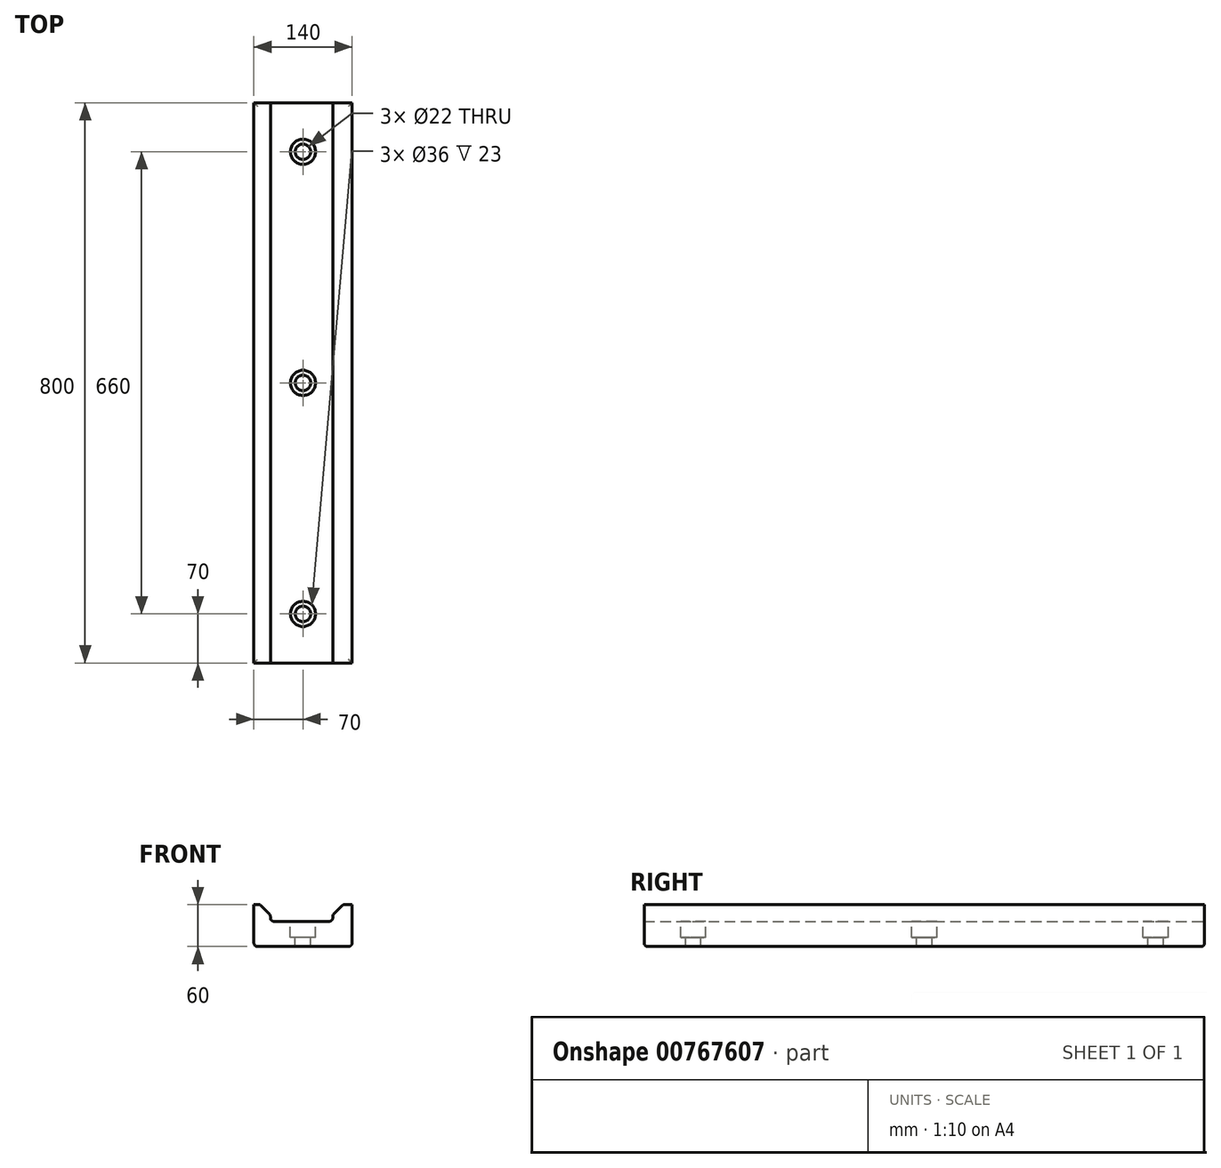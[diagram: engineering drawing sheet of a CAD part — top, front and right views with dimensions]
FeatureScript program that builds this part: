
annotation { "Feature Type Name" : "Feature", "Feature Type Description" : "" }
export const myFeature = defineFeature(function(context is Context, id is Id, definition is map)
    precondition{}
    {
        {
            var Q0;
            Q0=qCreatedBy(makeId("Front.planeOp"),FACE);
            var sketch = newSketch(context, id + "F0", { "sketchPlane" : qUnion([Q0])});
            skLineSegment(sketch, "E0.bottom", {"start": v(70, 30) * mm, "end": v(-70, 30) * mm});
            skLineSegment(sketch, "E0.top", {"start": v(70, -30) * mm, "end": v(-70, -30) * mm});
            skLineSegment(sketch, "E0.left", {"start": v(70, 30) * mm, "end": v(70, -30) * mm});
            skLineSegment(sketch, "E0.right", {"start": v(-70, 30) * mm, "end": v(-70, -30) * mm});
            skPoint(sketch, "E0.middle", {"position": v(0, 0) * mm});
            skLineSegment(sketch, "E1", {"start": v(-46.5, 6) * mm, "end": v(-46.5, 30) * mm});
            skLineSegment(sketch, "E2", {"start": v(42.5, 30) * mm, "end": v(42.5, 6) * mm});
            skLineSegment(sketch, "E3", {"start": v(-46.5, 6) * mm, "end": v(42.5, 6) * mm});
            skSolve(sketch);
        }
        {
            var Q0;
            Q0=makeQuery(id+"F0.imprint","IMPRINT",FACE,{"disambiguationData":[TD([[makeQuery(id+"F0.imprint","IMPRINT",EDGE,{"derivedFrom":sQuery(id+"F0.wireOp",EDGE,"E0.top")}),-1.0]])]});
            extrude(context, id + "F1", {"entities" : qUnion([Q0]), "depth" : 800 * mm, "offsetDistance" : 25 * mm});
        }
        {
            var Q0;
            Q0=makeQuery(id+"F1.opExtrude","SWEPT_EDGE",EDGE,{"disambiguationData":[OSD([sQuery(id+"F0.wireOp",EDGE,"E0.bottom"),sQuery(id+"F0.wireOp",EDGE,"E1")])]});
            var Q1;
            Q1=makeQuery(id+"F1.opExtrude","SWEPT_EDGE",EDGE,{"disambiguationData":[OSD([sQuery(id+"F0.wireOp",EDGE,"E0.bottom"),sQuery(id+"F0.wireOp",EDGE,"E2")])]});
            chamfer(context, id + "F2", {"entities" : qUnion([Q0, Q1]), "width" : 15 * mm, "tangentPropagation" : true});
        }
        {
            var Q0;
            {var subQ0=sQuery(id+"F0.wireOp",EDGE,"E0.bottom");var subQ1=sQuery(id+"F0.wireOp",EDGE,"E1");Q0=makeQuery(id+"F2.opChamfer","BLEND_EDGE",EDGE,{"blendedFrom":[makeQuery(id+"F1.opExtrude","SWEPT_EDGE",EDGE,{"disambiguationData":[OSD([subQ0,subQ1])]}),makeQuery(id+"F1.opExtrude","SWEPT_FACE",FACE,{"disambiguationData":[OSD([subQ0]),TDD([makeQuery(id+"F0.imprint","IMPRINT",EDGE,{"disambiguationData":[TD([[makeQuery(id+"F0.imprint","INTERSECT",VERTEX,{"derivedFrom":[subQ0,sQuery(id+"F0.wireOp",EDGE,"E0.right")]}),1.0]])],"derivedFrom":subQ0})])]})],"blendedInto":[makeQuery(id+"F1.opExtrude","SWEPT_FACE",FACE,{"disambiguationData":[OSD([subQ0]),TDD([makeQuery(id+"F0.imprint","IMPRINT",EDGE,{"disambiguationData":[TD([[makeQuery(id+"F0.imprint","INTERSECT",VERTEX,{"derivedFrom":[subQ0,sQuery(id+"F0.wireOp",EDGE,"E0.right")]}),1.0]])],"derivedFrom":subQ0})])]})]});}
            var Q1;
            {var subQ0=sQuery(id+"F0.wireOp",EDGE,"E1");Q1=makeQuery(id+"F2.opChamfer","BLEND_EDGE",EDGE,{"blendedFrom":[makeQuery(id+"F1.opExtrude","SWEPT_EDGE",EDGE,{"disambiguationData":[OSD([sQuery(id+"F0.wireOp",EDGE,"E0.bottom"),subQ0])]}),makeQuery(id+"F1.opExtrude","SWEPT_FACE",FACE,{"disambiguationData":[OSD([subQ0])]})],"blendedInto":[makeQuery(id+"F1.opExtrude","SWEPT_FACE",FACE,{"disambiguationData":[OSD([subQ0])]})]});}
            var Q2;
            Q2=makeQuery(id+"F1.opExtrude","SWEPT_EDGE",EDGE,{"disambiguationData":[OSD([sQuery(id+"F0.wireOp",EDGE,"E1"),sQuery(id+"F0.wireOp",EDGE,"E3")])]});
            var Q3;
            {var subQ0=sQuery(id+"F0.wireOp",EDGE,"E0.bottom");var subQ1=sQuery(id+"F0.wireOp",EDGE,"E2");Q3=makeQuery(id+"F2.opChamfer","BLEND_EDGE",EDGE,{"blendedFrom":[makeQuery(id+"F1.opExtrude","SWEPT_EDGE",EDGE,{"disambiguationData":[OSD([subQ0,subQ1])]}),makeQuery(id+"F1.opExtrude","SWEPT_FACE",FACE,{"disambiguationData":[OSD([subQ0]),TDD([makeQuery(id+"F0.imprint","IMPRINT",EDGE,{"disambiguationData":[TD([[makeQuery(id+"F0.imprint","INTERSECT",VERTEX,{"derivedFrom":[subQ0,sQuery(id+"F0.wireOp",EDGE,"E0.left")]}),-1.0]])],"derivedFrom":subQ0})])]})],"blendedInto":[makeQuery(id+"F1.opExtrude","SWEPT_FACE",FACE,{"disambiguationData":[OSD([subQ0]),TDD([makeQuery(id+"F0.imprint","IMPRINT",EDGE,{"disambiguationData":[TD([[makeQuery(id+"F0.imprint","INTERSECT",VERTEX,{"derivedFrom":[subQ0,sQuery(id+"F0.wireOp",EDGE,"E0.left")]}),-1.0]])],"derivedFrom":subQ0})])]})]});}
            var Q4;
            {var subQ0=sQuery(id+"F0.wireOp",EDGE,"E2");Q4=makeQuery(id+"F2.opChamfer","BLEND_EDGE",EDGE,{"blendedFrom":[makeQuery(id+"F1.opExtrude","SWEPT_EDGE",EDGE,{"disambiguationData":[OSD([sQuery(id+"F0.wireOp",EDGE,"E0.bottom"),subQ0])]}),makeQuery(id+"F1.opExtrude","SWEPT_FACE",FACE,{"disambiguationData":[OSD([subQ0])]})],"blendedInto":[makeQuery(id+"F1.opExtrude","SWEPT_FACE",FACE,{"disambiguationData":[OSD([subQ0])]})]});}
            var Q5;
            Q5=makeQuery(id+"F1.opExtrude","SWEPT_EDGE",EDGE,{"disambiguationData":[OSD([sQuery(id+"F0.wireOp",EDGE,"E2"),sQuery(id+"F0.wireOp",EDGE,"E3")])]});
            var Q6;
            Q6=makeQuery(id+"F1.opExtrude","SWEPT_EDGE",EDGE,{"disambiguationData":[OSD([sQuery(id+"F0.wireOp",EDGE,"E0.top"),sQuery(id+"F0.wireOp",EDGE,"E0.right")])]});
            var Q7;
            Q7=makeQuery(id+"F1.opExtrude","SWEPT_EDGE",EDGE,{"disambiguationData":[OSD([sQuery(id+"F0.wireOp",EDGE,"E0.top"),sQuery(id+"F0.wireOp",EDGE,"E0.left")])]});
            var Q8;
            Q8=makeQuery(id+"F1.opExtrude","CAP_EDGE",EDGE,{"disambiguationData":[OSD([sQuery(id+"F0.wireOp",EDGE,"E0.top")])],"isStart":false});
            var Q9;
            Q9=makeQuery(id+"F1.opExtrude","CAP_EDGE",EDGE,{"disambiguationData":[OSD([sQuery(id+"F0.wireOp",EDGE,"E0.top")])],"isStart":true});
            fillet(context, id + "F3", {"entities" : qUnion([Q0, Q1, Q2, Q3, Q4, Q5, Q6, Q7, Q8, Q9]), "radius" : 5 * mm, "tangentPropagation" : true, "allowEdgeOverflow" : false});
        }
        {
            var Q0;
            Q0=makeQuery(id+"F1.opExtrude","SWEPT_FACE",FACE,{"disambiguationData":[OSD([sQuery(id+"F0.wireOp",EDGE,"E3")])]});
            var sketch = newSketch(context, id + "F4", { "sketchPlane" : qUnion([Q0])});
            skCircle(sketch, "E4", {"center": v(0, -70) * mm, "radius": 10 * mm});
            skCircle(sketch, "E5", {"center": v(0, -730) * mm, "radius": 10 * mm});
            skCircle(sketch, "E6", {"center": v(0, -400) * mm, "radius": 10 * mm});
            skSolve(sketch);
        }
        {
            var Q0;
            Q0=sQuery(id+"F4.wireOp",VERTEX,"E4.center");
            var Q1;
            Q1=makeQuery(id+"F1.opExtrude","SWEPT_BODY",BODY,{"disambiguationData":[OSD([sQuery(id+"F0.wireOp",EDGE,"E0.bottom"),sQuery(id+"F0.wireOp",EDGE,"E0.top"),sQuery(id+"F0.wireOp",EDGE,"E0.left"),sQuery(id+"F0.wireOp",EDGE,"E0.right"),sQuery(id+"F0.wireOp",EDGE,"E1"),sQuery(id+"F0.wireOp",EDGE,"E2"),sQuery(id+"F0.wireOp",EDGE,"E3")])]});
            hole(context, id + "F5", {"style" : HoleStyle.C_BORE, "endStyle" : HoleEndStyle.THROUGH, "holeDiameter" : 22 * mm, "cBoreDiameter" : 36 * mm, "cBoreDepth" : 23 * mm, "majorDiameter" : 5 * mm, "isTappedThrough" : true, "tappedDepth" : 12 * mm, "tapClearance" : 3, "startFromSketch" : true, "locations" : qUnion([Q0]), "scope" : qUnion([Q1])});
        }
        {
            var Q0;
            Q0=sQuery(id+"F4.wireOp",VERTEX,"E6.center");
            var Q1;
            Q1=makeQuery(id+"F1.opExtrude","SWEPT_BODY",BODY,{"disambiguationData":[OSD([sQuery(id+"F0.wireOp",EDGE,"E0.bottom"),sQuery(id+"F0.wireOp",EDGE,"E0.top"),sQuery(id+"F0.wireOp",EDGE,"E0.left"),sQuery(id+"F0.wireOp",EDGE,"E0.right"),sQuery(id+"F0.wireOp",EDGE,"E1"),sQuery(id+"F0.wireOp",EDGE,"E2"),sQuery(id+"F0.wireOp",EDGE,"E3")])]});
            hole(context, id + "F6", {"style" : HoleStyle.C_BORE, "endStyle" : HoleEndStyle.THROUGH, "holeDiameter" : 22 * mm, "cBoreDiameter" : 36 * mm, "cBoreDepth" : 23 * mm, "majorDiameter" : 5 * mm, "isTappedThrough" : true, "tappedDepth" : 12 * mm, "tapClearance" : 3, "startFromSketch" : true, "locations" : qUnion([Q0]), "scope" : qUnion([Q1])});
        }
        {
            var Q0;
            Q0=sQuery(id+"F4.wireOp",VERTEX,"E5.center");
            var Q1;
            Q1=makeQuery(id+"F1.opExtrude","SWEPT_BODY",BODY,{"disambiguationData":[OSD([sQuery(id+"F0.wireOp",EDGE,"E0.bottom"),sQuery(id+"F0.wireOp",EDGE,"E0.top"),sQuery(id+"F0.wireOp",EDGE,"E0.left"),sQuery(id+"F0.wireOp",EDGE,"E0.right"),sQuery(id+"F0.wireOp",EDGE,"E1"),sQuery(id+"F0.wireOp",EDGE,"E2"),sQuery(id+"F0.wireOp",EDGE,"E3")])]});
            hole(context, id + "F7", {"style" : HoleStyle.C_BORE, "endStyle" : HoleEndStyle.THROUGH, "holeDiameter" : 22 * mm, "cBoreDiameter" : 36 * mm, "cBoreDepth" : 23 * mm, "majorDiameter" : 5 * mm, "isTappedThrough" : true, "tappedDepth" : 12 * mm, "tapClearance" : 3, "startFromSketch" : true, "locations" : qUnion([Q0]), "scope" : qUnion([Q1])});
        }
    });
